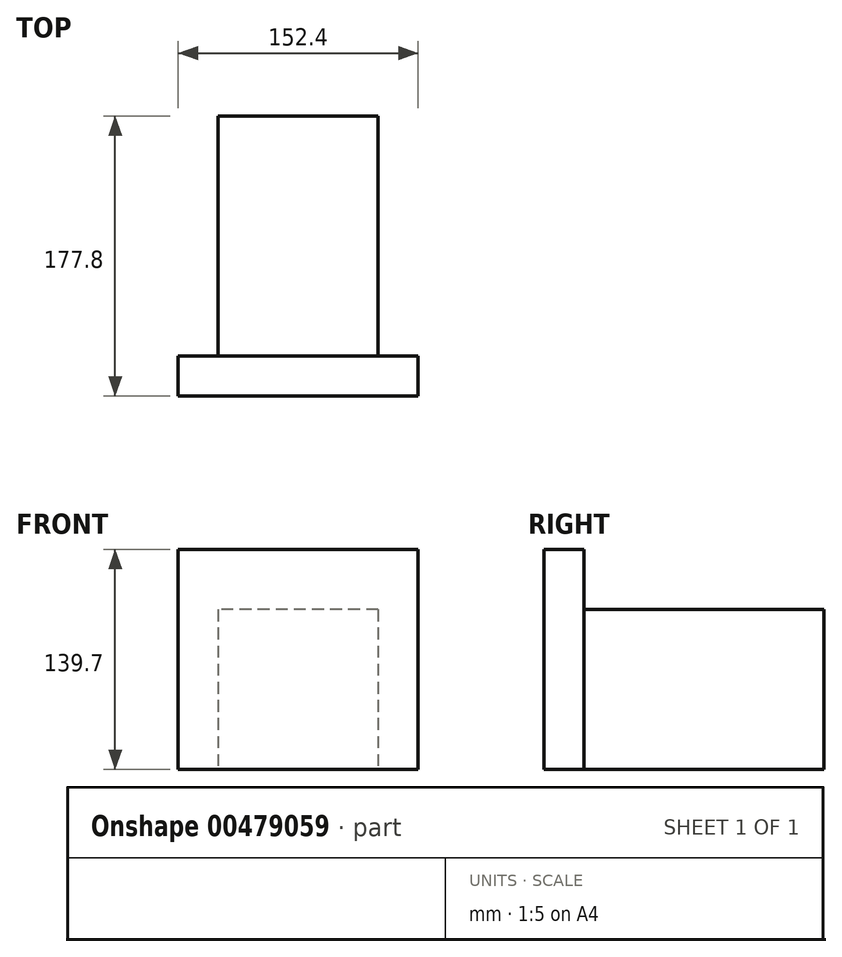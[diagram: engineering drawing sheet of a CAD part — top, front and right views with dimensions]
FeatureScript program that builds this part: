
annotation { "Feature Type Name" : "Feature", "Feature Type Description" : "" }
export const myFeature = defineFeature(function(context is Context, id is Id, definition is map)
    precondition{}
    {
        {
            var Q0;
            Q0=qCreatedBy(makeId("Top.planeOp"),FACE);
            var sketch = newSketch(context, id + "F0", { "sketchPlane" : qUnion([Q0])});
            skLineSegment(sketch, "E0.bottom", {"start": v(50.8, 76.2) * mm, "end": v(-50.8, 76.2) * mm});
            skLineSegment(sketch, "E0.top", {"start": v(50.8, -76.2) * mm, "end": v(-50.8, -76.2) * mm});
            skLineSegment(sketch, "E0.left", {"start": v(50.8, 76.2) * mm, "end": v(50.8, -76.2) * mm});
            skLineSegment(sketch, "E0.right", {"start": v(-50.8, 76.2) * mm, "end": v(-50.8, -76.2) * mm});
            skPoint(sketch, "E0.middle", {"position": v(0, 0) * mm});
            skSolve(sketch);
        }
        {
            var Q0;
            Q0 = qSketchRegion(id + "F0", true);
            extrude(context, id + "F1", {"entities" : qUnion([Q0]), "depth" : 101.6 * mm});
        }
        {
            var Q0;
            Q0=makeQuery(id+"F1.opExtrude","SWEPT_FACE",FACE,{"disambiguationData":[OSD([sQuery(id+"F0.wireOp",EDGE,"E0.top")])]});
            var sketch = newSketch(context, id + "F2", { "sketchPlane" : qUnion([Q0])});
            skLineSegment(sketch, "E1", {"start": v(-76.2, 0) * mm, "end": v(76.2, 0) * mm});
            skLineSegment(sketch, "E2", {"start": v(76.2, 0) * mm, "end": v(76.2, 139.7) * mm});
            skLineSegment(sketch, "E3", {"start": v(76.2, 139.7) * mm, "end": v(-76.2, 139.7) * mm});
            skLineSegment(sketch, "E4", {"start": v(-76.2, 139.7) * mm, "end": v(-76.2, 0) * mm});
            skSolve(sketch);
        }
        {
            var Q0;
            Q0 = qSketchRegion(id + "F2", true);
            extrude(context, id + "F3", {"entities" : qUnion([Q0]), "operationType" : NewBodyOperationType.ADD, "depth" : 25.4 * mm});
        }
    });
